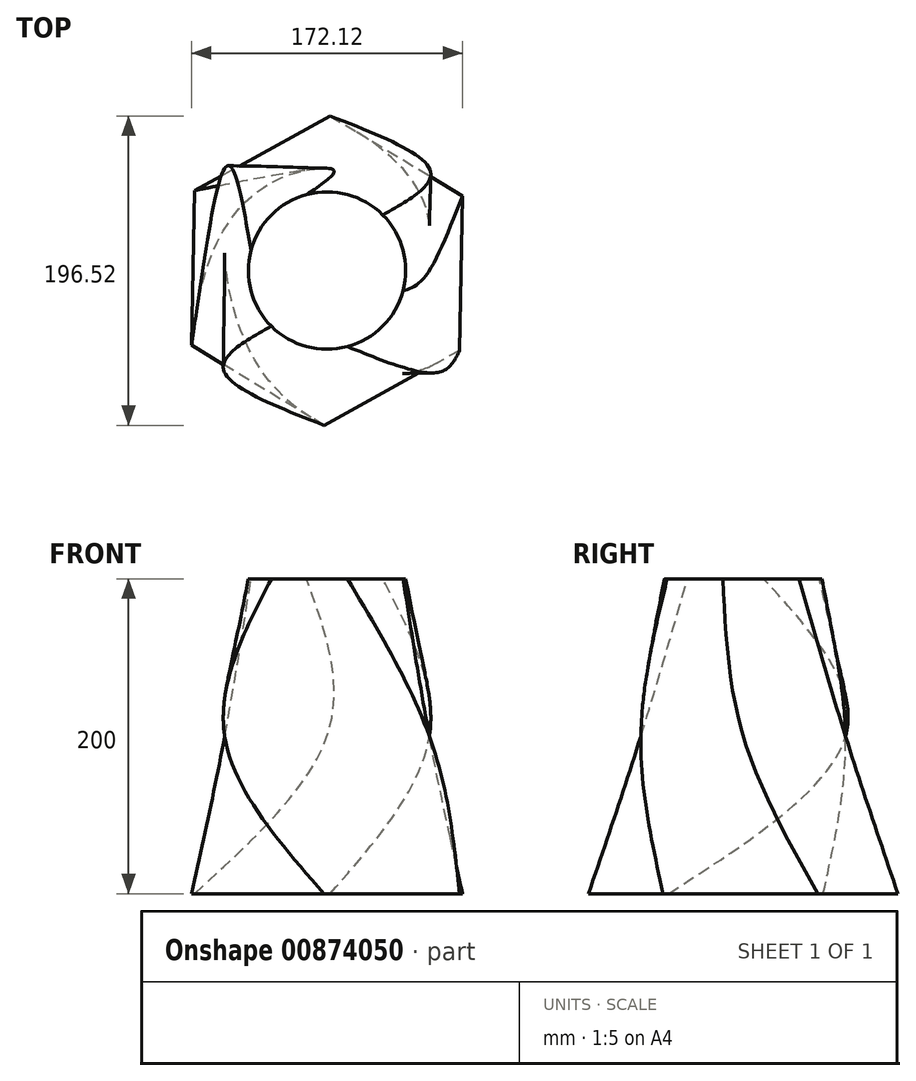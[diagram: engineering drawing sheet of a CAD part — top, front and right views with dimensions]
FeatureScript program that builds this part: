
annotation { "Feature Type Name" : "Feature", "Feature Type Description" : "" }
export const myFeature = defineFeature(function(context is Context, id is Id, definition is map)
    precondition{}
    {
        {
            var Q0;
            Q0=qCreatedBy(makeId("Top.planeOp"),FACE);
            cPlane(context, id + "F0", {"entities" : qUnion([Q0]), "cplaneType" : CPlaneType.OFFSET, "offset" : 100 * mm, "width" : 150 * mm, "height" : 150 * mm});
        }
        {
            var Q0;
            Q0=qCreatedBy(id+"F0.planeOp",FACE);
            var sketch = newSketch(context, id + "F1", { "sketchPlane" : qUnion([Q0])});
            skCircle(sketch, "E0", {"center": v(0, 0) * mm, "radius": 50 * mm});
            skSolve(sketch);
        }
        {
            var Q0;
            Q0=qCreatedBy(makeId("Top.planeOp"),FACE);
            var sketch = newSketch(context, id + "F2", { "sketchPlane" : qUnion([Q0])});
            skLineSegment(sketch, "E1.bottom", {"start": v(-65, -65) * mm, "end": v(65, -65) * mm});
            skLineSegment(sketch, "E1.top", {"start": v(-65, 65) * mm, "end": v(65, 65) * mm});
            skLineSegment(sketch, "E1.left", {"start": v(-65, -65) * mm, "end": v(-65, 65) * mm});
            skLineSegment(sketch, "E1.right", {"start": v(65, -65) * mm, "end": v(65, 65) * mm});
            skPoint(sketch, "E1.middle", {"position": v(0, 0) * mm});
            skSolve(sketch);
        }
        {
            var Q0;
            Q0=qCreatedBy(makeId("Top.planeOp"),FACE);
            cPlane(context, id + "F3", {"entities" : qUnion([Q0]), "cplaneType" : CPlaneType.OFFSET, "offset" : 100 * mm, "oppositeDirection" : true, "width" : 150 * mm, "height" : 150 * mm});
        }
        {
            var Q0;
            Q0=qCreatedBy(id+"F3.planeOp",FACE);
            var sketch = newSketch(context, id + "F4", { "sketchPlane" : qUnion([Q0])});
            skCircle(sketch, "E2.cCircle", {"center": v(0, 0) * mm, "radius": 85.11 * mm, "construction": true});
            skLineSegment(sketch, "E2.0", {"start": v(-1.94, -98.26) * mm, "end": v(-86.06, -47.45) * mm});
            skLineSegment(sketch, "E2.1", {"start": v(-86.06, -47.45) * mm, "end": v(-84.12, 50.8) * mm});
            skLineSegment(sketch, "E2.2", {"start": v(-84.12, 50.8) * mm, "end": v(1.94, 98.26) * mm});
            skLineSegment(sketch, "E2.3", {"start": v(1.94, 98.26) * mm, "end": v(86.06, 47.45) * mm});
            skLineSegment(sketch, "E2.4", {"start": v(86.06, 47.45) * mm, "end": v(84.12, -50.8) * mm});
            skLineSegment(sketch, "E2.5", {"start": v(84.12, -50.8) * mm, "end": v(-1.94, -98.26) * mm});
            skPoint(sketch, "E2.0.midPoint", {"position": v(-44, -72.85) * mm});
            skSolve(sketch);
        }
        {
            var Q0;
            Q0=makeQuery(id+"F4.imprint","IMPRINT",FACE,{"disambiguationData":[TD([[makeQuery(id+"F4.imprint","IMPRINT",EDGE,{"derivedFrom":sQuery(id+"F4.wireOp",EDGE,"E2.0")}),-1.0]])]});
            var Q1;
            Q1=makeQuery(id+"F2.imprint","IMPRINT",FACE,{"disambiguationData":[TD([[makeQuery(id+"F2.imprint","IMPRINT",EDGE,{"derivedFrom":sQuery(id+"F2.wireOp",EDGE,"E1.bottom")}),1.0]])]});
            var Q2;
            Q2=makeQuery(id+"F1.imprint","IMPRINT",FACE,{"disambiguationData":[TD([[makeQuery(id+"F1.imprint","IMPRINT",EDGE,{"derivedFrom":sQuery(id+"F1.wireOp",EDGE,"E0")}),1.0]])]});
            loft(context, id + "F5", {"sheetProfilesArray" : [{ "sheetProfileEntities" : qUnion([Q0]) }, { "sheetProfileEntities" : qUnion([Q1]) }, { "sheetProfileEntities" : qUnion([Q2]) }]});
        }
    });
